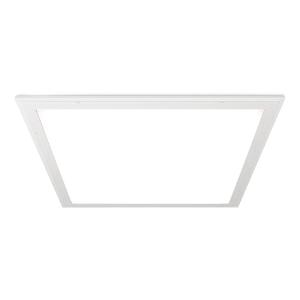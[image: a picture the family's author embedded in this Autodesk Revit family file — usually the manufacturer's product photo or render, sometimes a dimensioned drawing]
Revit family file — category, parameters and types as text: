
# Revit family: 3f_filippi_-_l_650_luce_diffusa_lgs_3f_filippi_-_21869_-_l_650_52w-940_dali_lgs_596x596
name_source: partatom
category: Lighting Fixtures
units: mm (PartAtom-declared; Revit-internal decimal feet)

## family parameters
Cut with Voids When Loaded = No
Host = Face
Light Source = No
Part Type = Normal
Room Calculation Point = No
Round Connector Dimension = Use Diameter
Shared = No

## types (1)
- 3F Filippi - L 650 Luce Diffusa LGS (1 x LED, 5551 lm, 57 W, 4000 K)
    Apparent Load = 57 VA
    Approval mark = ENEC
    CIE Flux Codes = 66 93 98 100 100
    Color Rendering = 90
    Color Temperature = 4000 K
    Control Gear = Electronic transformer
    Default Elevation = 1800 mm
    Description = ILLUMINOTECHNICAL
Luminous efficiency 100% (DLOR 100%, ULOR 0%).
Initial luminous flux of the luminaire 5551 lm.
Direct symmetric distribution.
Installation Interdistance Transv.D = 1.14 x hu - Long.D = 1.16 x hu.
Average luminance <3000 cd/m² for radial angles >65°.
Tabular UGR (CIE 117 - 4H-8H; S=0.25H; 70/50/20): RUG 18.2 - 18.1.
Beam angle: 85° - 85°.
Luminous efficacy 97 lm/W.
Lifetime (L93/B10): 30000 h. (tq+25°C)
Lifetime (L90/B10): 50000 h. (tq+25°C)
Lifetime (L85/B10): 80000 h. (tq+25°C)
Lifetime (L80/B10): 100000 h. (tq+25°C)
Sudden decreased luminous flux after 50000 hours: 0% (C0).
Photobiological safety in compliance with IEC/TR 62778: RG0 risk exempt, (IEC 62471).
In compliance with IEC/EN 62722-2-1 - IEC/EN 62717 standards.

SOURCE
Squared LED module 52W/940.
Source with special protection against aggressive chemically-volatile substances for standard LED technology.
Energy efficiency class (UE 2019/2020 - UE 2019/2015): E.
CIE 13.3 Colour rendering index: CRI >90 (R9 >50%).
IES TM-30 Fidelity Index: Rf = 92 Rg = 101.
CCT nominal colour temperature 4000 K.
Colour initial tolerance (MacAdam): SDCM 3.

MECHANICAL
Housing in galvannealed steel, painted in white epoxy-polyester.
Perimetral frame in white stainless steel.
LGS micro-prismatic flat diffuser in transparent methacrylate (PMMA), multi-lenticular exterior, anti-glare.
Anti-glare opal polycarbonate filter for brightness uniformity.
Luminaire with limited surface temperature. - D - (EN 60598-2-24)
Dimensions: 596x596 mm, height 90 mm. Weight 5.985 kg.
IP66 protection degree for exposed part, IP64 for recessed part.
Mechanical strength to impacts IK06 (1 joule).
Glow-wire test resistance 650°C.

ELECTRICAL
Halogen Free DALI-2 DATI (Parts 251, 252, 253), PUSH-DIM, electronic wiring 230V-50/60Hz, power factor 0.95 at full load, THD <25%, constant output current, SELV, class I, 1 driver, 1 DALI addresse.
Power of the luminaire 57 W.
CE - IEC 60598-1 - EN 60598-1.
SAFE FLICKER: PstLM=<1 and SVM=<0.4 (IEC TR 61547-1 and IEC TR 63158), to ensure a more comfortable and safe light.
Luminaire compliant with EN 60598-2-22 for power supply from a centralised emergency system CPSS (Central Power Supply System), not incorporated in the luminaire - high risk areas excluded. The default power and flux are 100% in AC and 15% in DC.
Ambient temperature from 0°C to +40°C.
Temperature class T6 max 85°C.
5-pole terminal block (L-N-PE-DA/DA) quick connection for line connection with connection capacity 2x2.5 mm² per poles.
Relative humidity UR: <85%.

INSTALLATION
Lay-in recessed fitting.
All accessories dedicated to this product are available on the Catalog and on our website www.3F-Filippi.com.

APPLICATIONS
Suitable product for food production plants (HACCP), IFS (Food Version 6), BRC (GSFS Food Version 7).
Environments: hospital premises, transit areas, laboratories, platform-roof, underpasses.
Environments: sterilized, aseptic.
In hospital environments, food industry or machines with parts in motion, with considerable sudden temperature changes, and in general in any environments requiring total protection against falling fragments, use luminaires with laminated glass only.
Tempered glass is not immune to falling fragments from harmless and caused by shocks or exceptionally derived from the tempering process.
Environments requiring a high level of protection and simplified cleaning.
Environments with exacting visual tasks, where diffused soft light for optimum visual comfort is required.

LIGHT MANAGEMENT
Recommended minimum setting: 10%.
The luminaire, equipped with (DALI-2 DATI) driver, can be controlled manually with 3F Easy Dim technology or automatically/manually with wired or wireless DALI/D2D control systems.
The D2D driver guarantees interoperability with other devices with the same certification by making the following information available:
Device Data (Part 251), Energy Report (Part 252), Diagnosis & Maintenance (Part 253).
In electrical systems without a regulation system (manual or automatic) and DALI bus, a suitable jumper must be made on the DA-DA terminals of the appliance.

WARNING
Luminaire designed for disposal/recycling at end-of-life.
Replaceable (LED only) light source by a professional. Replaceable control gear by a professional.
    Height = 0 mm  [stored 0 ft]
    Lamp = 1 x LED
    Lamp Light Flux = 5551 lm
    Lamp Power = 57 W
    Lamp count = 1
    Length = 596 mm
    Lifetime = 50000 h
    Luminous efficacy = 97 lm/W
    Manufacturer = 3F Filippi
    ModVariant = No
    Model = 3F Filippi - 21869 - L 650 52W-940 DALI LGS 596x596
    Mounting Place = Ceiling
    Mounting Type = Recessed
    Number of Poles = 1
    OnlyDefault = Yes
    Power Factor = 1
    Product Name = 3F Filippi - L 650 Luce Diffusa LGS
    Product group = recessed luminaire
    ProductGroupID = 4
    Protection Class = Protection class I
    Protection Degree = IP 64
    RLX_Detail_Level = 1
    RLX_Emergency_Light_Flux = 0 lm
    RLX_Emergency_Type = 0
    RLX_Emergency_Type_DB = No
    RlxData = <blob elided: 100889 chars, md5=f6d91ee7>
    Socket = socket
    Standby Power = 0 W
    System Light Flux = 5551 lm
    System Power = 57 W
    Type Comments = Product without accessories
    Type Image = 3ffilippi_l_650_luce_diffusa_lgs.jpg
    URL = http://relux.com
    VarID = ---
    Voltage = 0 V
    Weight = 0.00 kg
    Width = 596 mm

note: [stored X ft] marks values corroborated as IEEE doubles in the binary element streams (Revit-internal decimal feet)

## geometry (parser evidence)
native form markers: Blend x4, Sweep x11
no freeform markers — native parametric forms only
